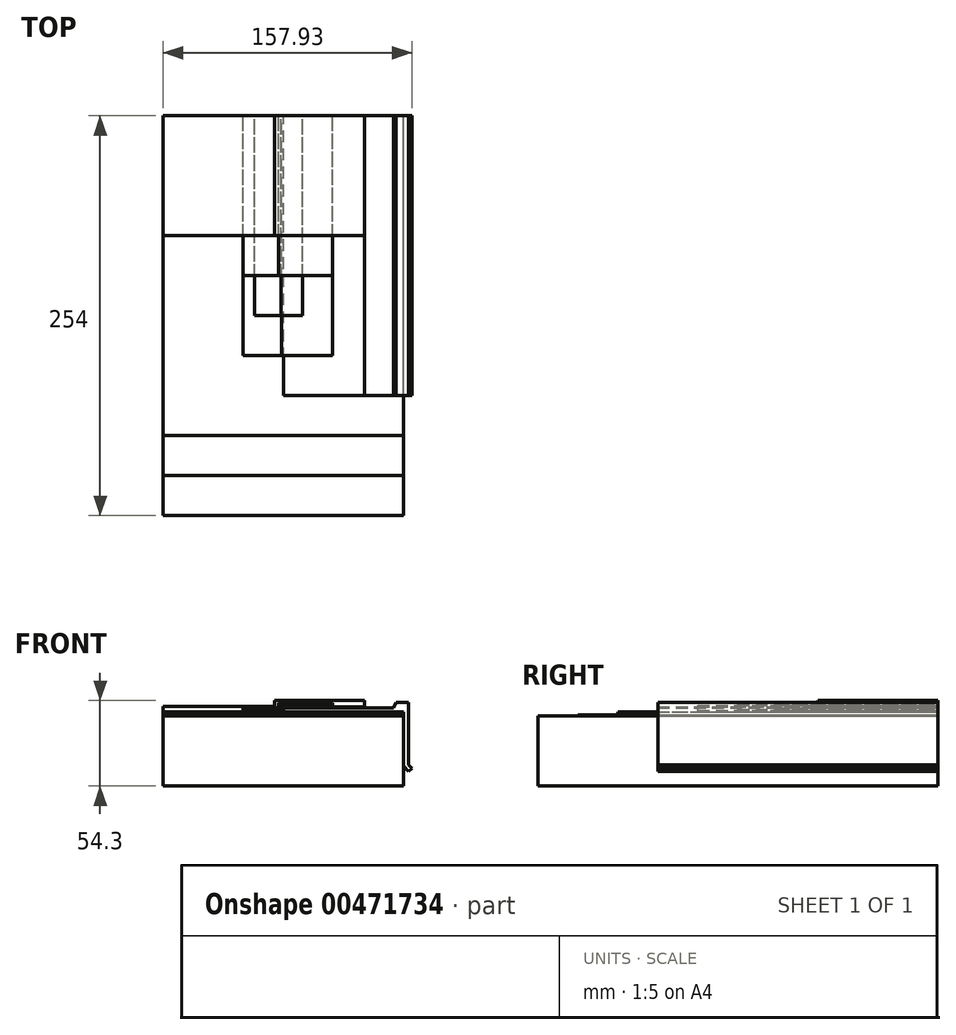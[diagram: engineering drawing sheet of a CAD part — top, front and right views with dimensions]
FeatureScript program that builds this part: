
annotation { "Feature Type Name" : "Feature", "Feature Type Description" : "" }
export const myFeature = defineFeature(function(context is Context, id is Id, definition is map)
    precondition{}
    {
        {
            var Q0;
            Q0=qCreatedBy(makeId("Front.planeOp"),FACE);
            var sketch = newSketch(context, id + "F0", { "sketchPlane" : qUnion([Q0])});
            skLineSegment(sketch, "E0.bottom", {"start": v(-76.44, 23.51) * mm, "end": v(76.17, 23.51) * mm});
            skLineSegment(sketch, "E0.top", {"start": v(-76.44, -21.14) * mm, "end": v(76.17, -21.14) * mm});
            skLineSegment(sketch, "E0.left", {"start": v(-76.44, 23.51) * mm, "end": v(-76.44, -21.14) * mm});
            skLineSegment(sketch, "E0.right", {"start": v(76.17, 23.51) * mm, "end": v(76.17, -21.14) * mm});
            skLineSegment(sketch, "E1", {"start": v(-76.44, 23.51) * mm, "end": v(-76.44, 24.02) * mm});
            skLineSegment(sketch, "E2", {"start": v(-76.44, 24.02) * mm, "end": v(76.17, 24.02) * mm});
            skLineSegment(sketch, "E3", {"start": v(76.17, 24.02) * mm, "end": v(76.17, 23.51) * mm});
            skLineSegment(sketch, "E4", {"start": v(-76.44, 24.02) * mm, "end": v(-76.44, 26.05) * mm});
            skLineSegment(sketch, "E5", {"start": v(-76.44, 26.05) * mm, "end": v(76.17, 26.05) * mm});
            skLineSegment(sketch, "E6", {"start": v(76.17, 26.05) * mm, "end": v(76.17, 24.02) * mm});
            skLineSegment(sketch, "E7", {"start": v(-0.13, 26.05) * mm, "end": v(-0.13, 28.6) * mm});
            skLineSegment(sketch, "E8", {"start": v(-0.13, 28.6) * mm, "end": v(69.71, 28.6) * mm});
            skLineSegment(sketch, "E9", {"start": v(69.71, 28.6) * mm, "end": v(71.44, 31.9) * mm});
            skLineSegment(sketch, "E10", {"start": v(71.44, 31.9) * mm, "end": v(79.33, 31.9) * mm});
            skLineSegment(sketch, "E11", {"start": v(79.33, 31.9) * mm, "end": v(79.33, -7.54) * mm});
            skLineSegment(sketch, "E12", {"start": v(79.33, -7.54) * mm, "end": v(81.49, -9.98) * mm});
            skLineSegment(sketch, "E13", {"start": v(81.49, -9.98) * mm, "end": v(79.33, -11.88) * mm});
            skLineSegment(sketch, "E14", {"start": v(79.33, -11.88) * mm, "end": v(76.17, -8.3) * mm});
            skLineSegment(sketch, "E15", {"start": v(-0.13, 28.6) * mm, "end": v(-0.13, 29.1) * mm});
            skLineSegment(sketch, "E16", {"start": v(-0.13, 29.1) * mm, "end": v(51.34, 29.1) * mm});
            skLineSegment(sketch, "E17", {"start": v(51.34, 29.1) * mm, "end": v(51.34, 28.6) * mm});
            skLineSegment(sketch, "E18", {"start": v(-25.62, 26.05) * mm, "end": v(-25.62, 27.07) * mm});
            skLineSegment(sketch, "E19", {"start": v(-25.62, 27.07) * mm, "end": v(-1.15, 27.07) * mm});
            skLineSegment(sketch, "E20", {"start": v(-1.15, 27.07) * mm, "end": v(-1.15, 30.12) * mm});
            skLineSegment(sketch, "E21", {"start": v(-1.15, 30.12) * mm, "end": v(30.95, 30.12) * mm});
            skLineSegment(sketch, "E22", {"start": v(30.95, 30.12) * mm, "end": v(30.95, 29.1) * mm});
            skLineSegment(sketch, "E23", {"start": v(-18.44, 27.07) * mm, "end": v(-18.44, 27.58) * mm});
            skLineSegment(sketch, "E24", {"start": v(-18.44, 27.58) * mm, "end": v(-1.66, 27.58) * mm});
            skLineSegment(sketch, "E25", {"start": v(-1.66, 27.58) * mm, "end": v(-1.66, 30.62) * mm});
            skLineSegment(sketch, "E26", {"start": v(-1.66, 30.62) * mm, "end": v(12, 30.62) * mm});
            skLineSegment(sketch, "E27", {"start": v(12, 30.62) * mm, "end": v(12, 30.12) * mm});
            skLineSegment(sketch, "E28", {"start": v(-25.62, 27.07) * mm, "end": v(-25.62, 28.6) * mm});
            skLineSegment(sketch, "E29", {"start": v(-25.62, 28.6) * mm, "end": v(-3.18, 28.6) * mm});
            skLineSegment(sketch, "E30", {"start": v(-3.18, 28.6) * mm, "end": v(-3.18, 31.64) * mm});
            skLineSegment(sketch, "E31", {"start": v(-3.18, 31.64) * mm, "end": v(30.95, 31.64) * mm});
            skLineSegment(sketch, "E32", {"start": v(30.95, 31.64) * mm, "end": v(30.95, 30.12) * mm});
            skLineSegment(sketch, "E33", {"start": v(-1.15, 27.07) * mm, "end": v(-0.13, 27.07) * mm, "construction": true});
            skLineSegment(sketch, "E34", {"start": v(-1.66, 27.58) * mm, "end": v(-1.15, 27.58) * mm, "construction": true});
            skLineSegment(sketch, "E35", {"start": v(-3.18, 28.6) * mm, "end": v(-1.66, 28.6) * mm, "construction": true});
            skLineSegment(sketch, "E36", {"start": v(-76.44, 26.05) * mm, "end": v(-76.44, 29.6) * mm});
            skLineSegment(sketch, "E37", {"start": v(-76.44, 29.6) * mm, "end": v(-5.78, 29.6) * mm});
            skLineSegment(sketch, "E38", {"start": v(-5.78, 29.6) * mm, "end": v(-5.78, 33.16) * mm});
            skLineSegment(sketch, "E39", {"start": v(-5.78, 33.16) * mm, "end": v(51.3, 33.16) * mm});
            skLineSegment(sketch, "E40", {"start": v(51.3, 33.16) * mm, "end": v(51.34, 29.1) * mm});
            skLineSegment(sketch, "E41", {"start": v(-5.78, 29.6) * mm, "end": v(-5.78, 26.05) * mm, "construction": true});
            skSolve(sketch);
        }
        {
            var Q0;
            {var subQ1=sQuery(id+"F0.wireOp",EDGE,"E0.bottom");Q0=makeQuery(id+"F0.imprint","IMPRINT",FACE,{"disambiguationData":[TD([[makeQuery(id+"F0.imprint","IMPRINT",EDGE,{"derivedFrom":subQ1}),-1.0]])]});}
            extrude(context, id + "F1", {"entities" : qUnion([Q0]), "depth" : 254 * mm});
        }
        {
            var Q0;
            Q0=makeQuery(id+"F0.imprint","IMPRINT",FACE,{"disambiguationData":[TD([[makeQuery(id+"F0.imprint","IMPRINT",EDGE,{"derivedFrom":sQuery(id+"F0.wireOp",EDGE,"E0.bottom")}),1.0]])]});
            extrude(context, id + "F2", {"entities" : qUnion([Q0]), "depth" : 228.6 * mm});
        }
        {
            var Q0;
            Q0=makeQuery(id+"F0.imprint","IMPRINT",FACE,{"disambiguationData":[TD([[makeQuery(id+"F0.imprint","IMPRINT",EDGE,{"derivedFrom":sQuery(id+"F0.wireOp",EDGE,"E2")}),1.0]])]});
            extrude(context, id + "F3", {"entities" : qUnion([Q0]), "depth" : 203.2 * mm});
        }
        {
            var Q0;
            {var subQ4=sQuery(id+"F0.wireOp",EDGE,"E3");Q0=makeQuery(id+"F0.imprint","IMPRINT",FACE,{"disambiguationData":[TD([[makeQuery(id+"F0.imprint","IMPRINT",EDGE,{"derivedFrom":subQ4}),1.0]])]});}
            extrude(context, id + "F4", {"entities" : qUnion([Q0]), "depth" : 177.8 * mm});
        }
        {
            var Q0;
            {var subQ1=sQuery(id+"F0.wireOp",EDGE,"E15");Q0=makeQuery(id+"F0.imprint","IMPRINT",FACE,{"disambiguationData":[TD([[makeQuery(id+"F0.imprint","IMPRINT",EDGE,{"derivedFrom":subQ1}),-1.0]])]});}
            extrude(context, id + "F5", {"entities" : qUnion([Q0]), "depth" : 177.8 * mm});
        }
        {
            var Q0;
            {var subQ7=sQuery(id+"F0.wireOp",EDGE,"E7");Q0=makeQuery(id+"F0.imprint","IMPRINT",FACE,{"disambiguationData":[TD([[makeQuery(id+"F0.imprint","IMPRINT",EDGE,{"derivedFrom":subQ7}),1.0]])]});}
            extrude(context, id + "F6", {"entities" : qUnion([Q0]), "depth" : 152.4 * mm});
        }
        {
            var Q0;
            {var subQ1=sQuery(id+"F0.wireOp",EDGE,"E20");Q0=makeQuery(id+"F0.imprint","IMPRINT",FACE,{"disambiguationData":[TD([[makeQuery(id+"F0.imprint","IMPRINT",EDGE,{"derivedFrom":subQ1}),1.0]])]});}
            extrude(context, id + "F7", {"entities" : qUnion([Q0]), "depth" : 127 * mm});
        }
        {
            var Q0;
            {var subQ3=sQuery(id+"F0.wireOp",EDGE,"E23");Q0=makeQuery(id+"F0.imprint","IMPRINT",FACE,{"disambiguationData":[TD([[makeQuery(id+"F0.imprint","IMPRINT",EDGE,{"derivedFrom":subQ3}),1.0]])]});}
            extrude(context, id + "F8", {"entities" : qUnion([Q0]), "depth" : 101.6 * mm});
        }
        {
            var Q0;
            {var subQ2=sQuery(id+"F0.wireOp",EDGE,"E18");Q0=makeQuery(id+"F0.imprint","IMPRINT",FACE,{"disambiguationData":[TD([[makeQuery(id+"F0.imprint","IMPRINT",EDGE,{"derivedFrom":subQ2}),1.0]])]});}
            extrude(context, id + "F9", {"entities" : qUnion([Q0]), "depth" : 76.2 * mm});
        }
    });
